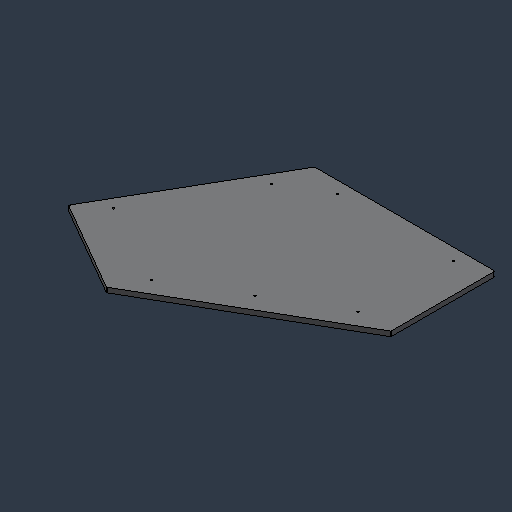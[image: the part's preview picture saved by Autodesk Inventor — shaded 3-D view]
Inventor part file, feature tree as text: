
AUTODESK INVENTOR PART (.ipt)
format: ipt  version: 2024.3 (Build 283343000, 343)  size: 88,064 bytes
history: native  units: mm (DEFAULTED — no unit token found)
features: fillet x1
ambient origin geometry x8: Origin, YZ Plane, XZ Plane, XY Plane, X Axis, Y Axis, Z Axis, Center Point
bodies: Solid1 (feature_tree)
feature tree (1):
  fillet  "Fillet1"  [1 undecoded]
note: 1 required parameter value undecoded (feature->parameter linkage not recoverable at this tier; creation-order binding heuristic only, values carry confidence <= 0.55)
